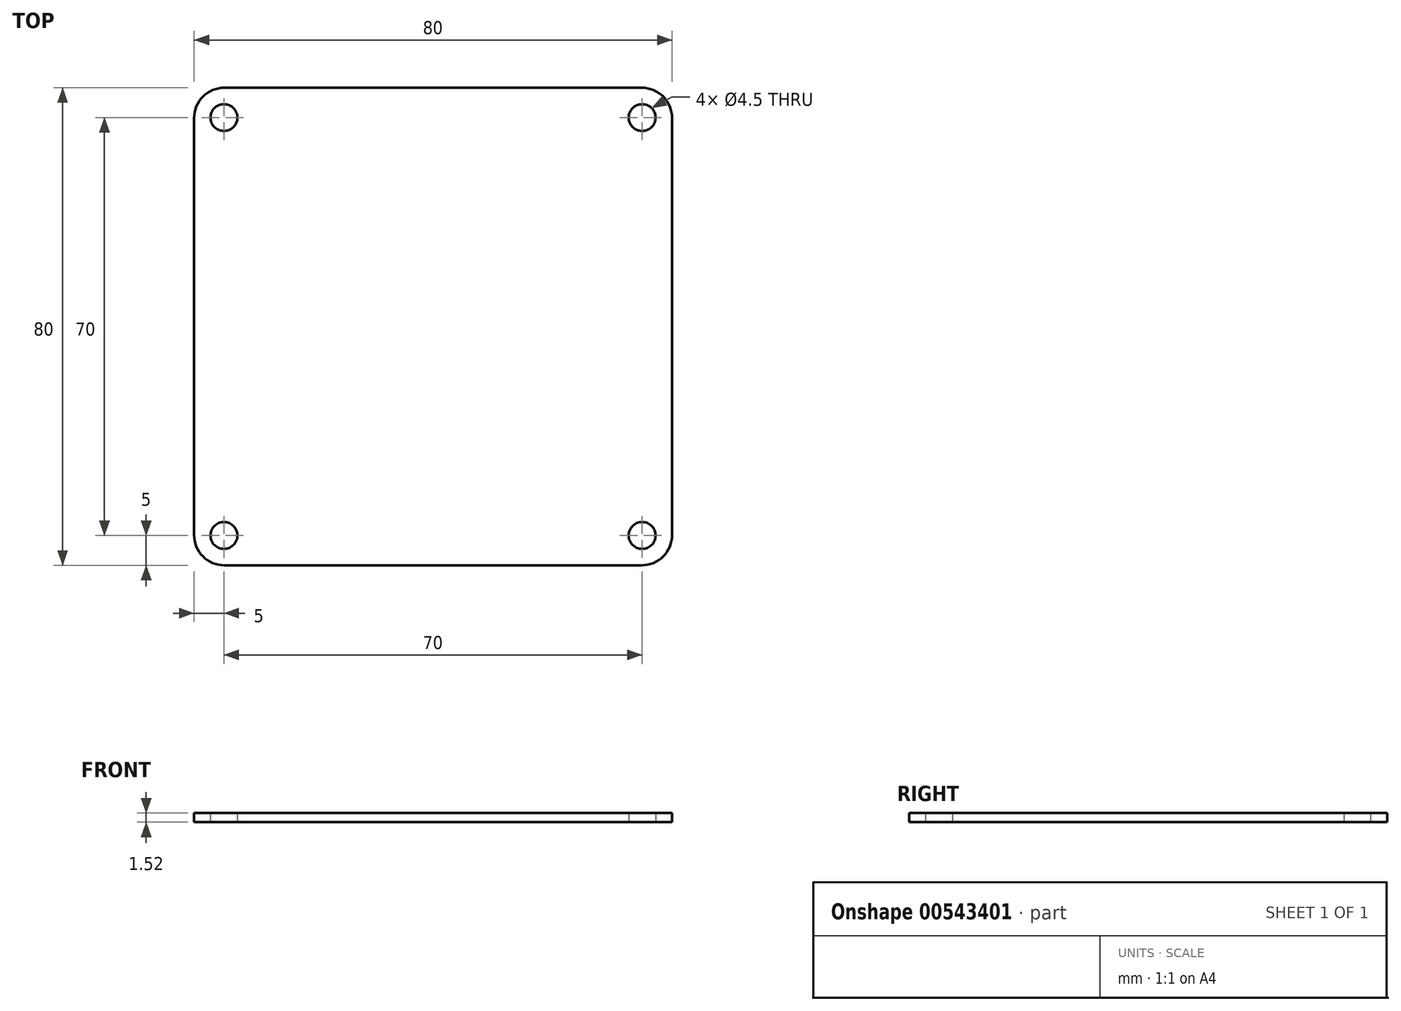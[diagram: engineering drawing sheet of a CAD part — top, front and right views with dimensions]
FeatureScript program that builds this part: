
annotation { "Feature Type Name" : "Feature", "Feature Type Description" : "" }
export const myFeature = defineFeature(function(context is Context, id is Id, definition is map)
    precondition{}
    {
        {
            var Q0;
            Q0=qCreatedBy(makeId("Top.planeOp"),FACE);
            var sketch = newSketch(context, id + "F0", { "sketchPlane" : qUnion([Q0])});
            skLineSegment(sketch, "E0.bottom", {"start": v(-40, 40) * mm, "end": v(40, 40) * mm});
            skLineSegment(sketch, "E0.top", {"start": v(-40, -40) * mm, "end": v(40, -40) * mm});
            skLineSegment(sketch, "E0.left", {"start": v(-40, 40) * mm, "end": v(-40, -40) * mm});
            skLineSegment(sketch, "E0.right", {"start": v(40, 40) * mm, "end": v(40, -40) * mm});
            skPoint(sketch, "E0.middle", {"position": v(0, 0) * mm});
            skCircle(sketch, "E1", {"center": v(-35, 35) * mm, "radius": 2.25 * mm});
            skCircle(sketch, "E2", {"center": v(35, 35) * mm, "radius": 2.25 * mm});
            skCircle(sketch, "E3", {"center": v(-35, -35) * mm, "radius": 2.25 * mm});
            skCircle(sketch, "E4", {"center": v(35, -35) * mm, "radius": 2.25 * mm});
            skLineSegment(sketch, "E5", {"start": v(-40, 0) * mm, "end": v(40, 0) * mm, "construction": true});
            skLineSegment(sketch, "E6", {"start": v(0, 40) * mm, "end": v(0, -40) * mm, "construction": true});
            skSolve(sketch);
        }
        {
            var Q0;
            Q0 = qSketchRegion(id + "F0", true);
            extrude(context, id + "F1", {"entities" : qUnion([Q0]), "endBound" : BoundingType.SYMMETRIC, "depth" : 1.52 * mm, "offsetDistance" : 25.4 * mm});
        }
        {
            var Q0;
            Q0=makeQuery(id+"F1.opExtrude","SWEPT_EDGE",EDGE,{"disambiguationData":[OSD([sQuery(id+"F0.wireOp",EDGE,"E0.top"),sQuery(id+"F0.wireOp",EDGE,"E0.left")])]});
            var Q1;
            Q1=makeQuery(id+"F1.opExtrude","SWEPT_EDGE",EDGE,{"disambiguationData":[OSD([sQuery(id+"F0.wireOp",EDGE,"E0.bottom"),sQuery(id+"F0.wireOp",EDGE,"E0.left")])]});
            var Q2;
            Q2=makeQuery(id+"F1.opExtrude","SWEPT_EDGE",EDGE,{"disambiguationData":[OSD([sQuery(id+"F0.wireOp",EDGE,"E0.bottom"),sQuery(id+"F0.wireOp",EDGE,"E0.right")])]});
            var Q3;
            Q3=makeQuery(id+"F1.opExtrude","SWEPT_EDGE",EDGE,{"disambiguationData":[OSD([sQuery(id+"F0.wireOp",EDGE,"E0.top"),sQuery(id+"F0.wireOp",EDGE,"E0.right")])]});
            fillet(context, id + "F2", {"entities" : qUnion([Q0, Q1, Q2, Q3]), "radius" : 5.08 * mm, "tangentPropagation" : true, "allowEdgeOverflow" : false});
        }
    });
